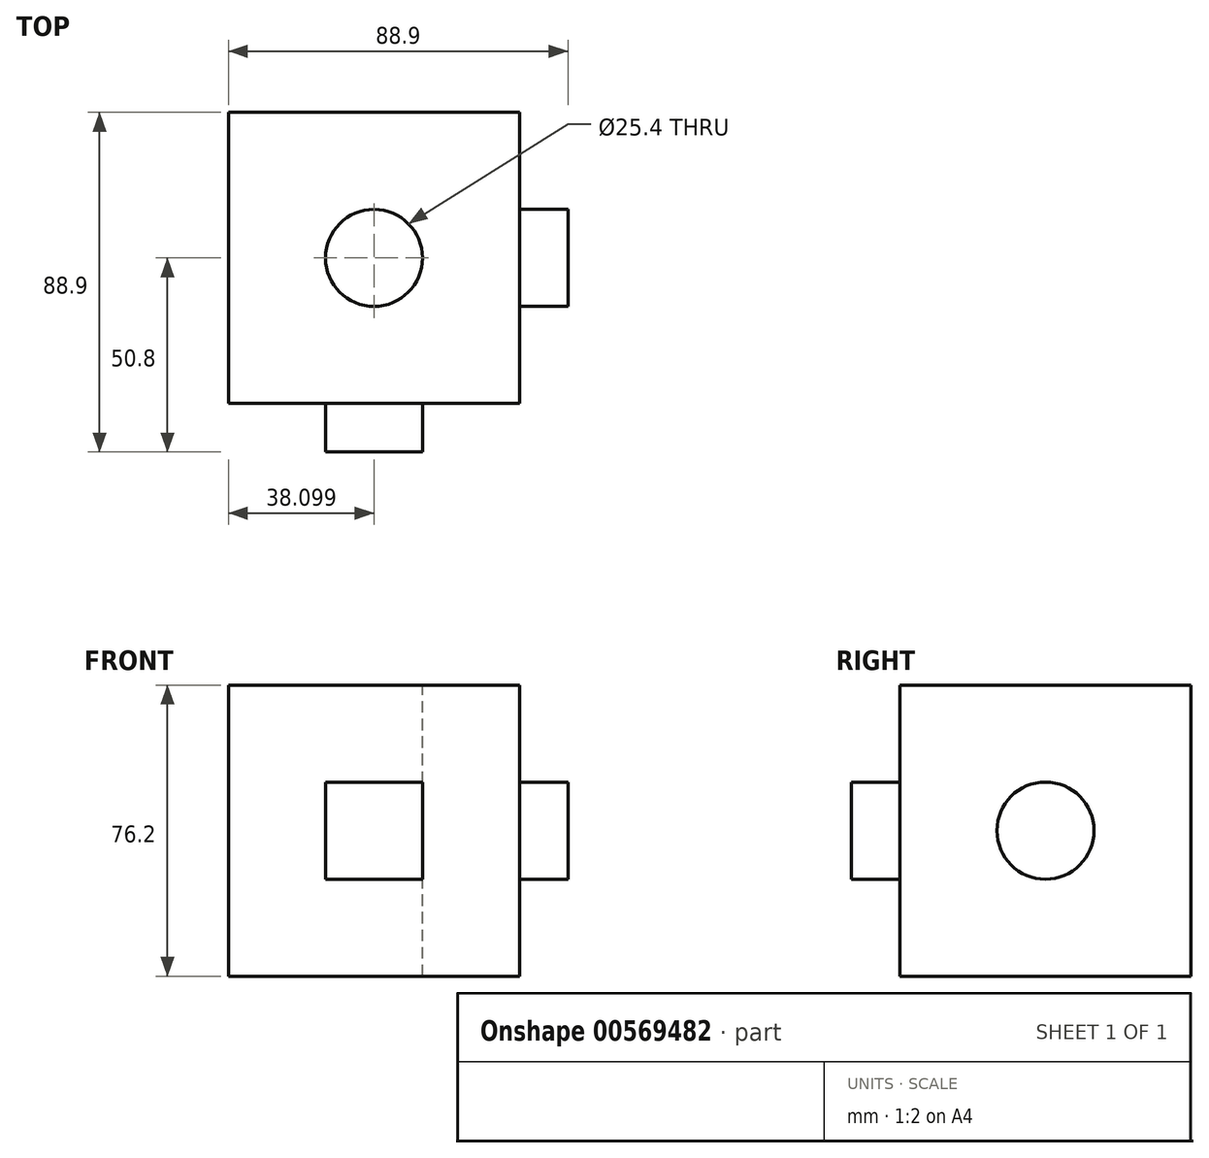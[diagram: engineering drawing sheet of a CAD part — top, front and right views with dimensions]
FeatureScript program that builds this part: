
annotation { "Feature Type Name" : "Feature", "Feature Type Description" : "" }
export const myFeature = defineFeature(function(context is Context, id is Id, definition is map)
    precondition{}
    {
        {
            var Q0;
            Q0=qCreatedBy(makeId("Front.planeOp"),FACE);
            var sketch = newSketch(context, id + "F0", { "sketchPlane" : qUnion([Q0])});
            skLineSegment(sketch, "E0.bottom", {"start": v(-26.71, 108.82) * mm, "end": v(49.49, 108.82) * mm});
            skLineSegment(sketch, "E0.top", {"start": v(-26.71, 32.62) * mm, "end": v(49.49, 32.62) * mm});
            skLineSegment(sketch, "E0.left", {"start": v(-26.71, 108.82) * mm, "end": v(-26.71, 32.62) * mm});
            skLineSegment(sketch, "E0.right", {"start": v(49.49, 108.82) * mm, "end": v(49.49, 32.62) * mm});
            skSolve(sketch);
        }
        {
            var Q0;
            Q0=makeQuery(id+"F0.imprint","IMPRINT",FACE,{"disambiguationData":[TD([[makeQuery(id+"F0.imprint","IMPRINT",EDGE,{"derivedFrom":sQuery(id+"F0.wireOp",EDGE,"E0.bottom")}),-1.0]])]});
            extrude(context, id + "F1", {"entities" : qUnion([Q0]), "depth" : 76.2 * mm, "offsetDistance" : 25.4 * mm});
        }
        {
            var Q0;
            Q0=makeQuery(id+"F1.opExtrude","CAP_FACE",FACE,{"disambiguationData":[OSD([sQuery(id+"F0.wireOp",EDGE,"E0.bottom"),sQuery(id+"F0.wireOp",EDGE,"E0.top"),sQuery(id+"F0.wireOp",EDGE,"E0.left"),sQuery(id+"F0.wireOp",EDGE,"E0.right")])],"isStart":false});
            var sketch = newSketch(context, id + "F2", { "sketchPlane" : qUnion([Q0])});
            skLineSegment(sketch, "E1.bottom", {"start": v(-1.31, 83.42) * mm, "end": v(24.09, 83.42) * mm});
            skLineSegment(sketch, "E1.top", {"start": v(-1.31, 58.02) * mm, "end": v(24.09, 58.02) * mm});
            skLineSegment(sketch, "E1.left", {"start": v(-1.31, 83.42) * mm, "end": v(-1.31, 58.02) * mm});
            skLineSegment(sketch, "E1.right", {"start": v(24.09, 83.42) * mm, "end": v(24.09, 58.02) * mm});
            skSolve(sketch);
        }
        {
            var Q0;
            Q0=makeQuery(id+"F2.imprint","IMPRINT",FACE,{"disambiguationData":[TD([[makeQuery(id+"F2.imprint","IMPRINT",EDGE,{"derivedFrom":sQuery(id+"F2.wireOp",EDGE,"E1.bottom")}),-1.0]])]});
            extrude(context, id + "F3", {"entities" : qUnion([Q0]), "operationType" : NewBodyOperationType.ADD, "depth" : 12.7 * mm, "offsetDistance" : 25.4 * mm});
        }
        {
            var Q0;
            Q0=makeQuery(id+"F1.opExtrude","SWEPT_FACE",FACE,{"disambiguationData":[OSD([sQuery(id+"F0.wireOp",EDGE,"E0.right")])]});
            var sketch = newSketch(context, id + "F4", { "sketchPlane" : qUnion([Q0])});
            skCircle(sketch, "E2", {"center": v(-38.1, 70.72) * mm, "radius": 12.7 * mm});
            skSolve(sketch);
        }
        {
            var Q0;
            Q0 = qSketchRegion(id + "F4", true);
            extrude(context, id + "F5", {"entities" : qUnion([Q0]), "operationType" : NewBodyOperationType.ADD, "depth" : 12.7 * mm, "offsetDistance" : 25.4 * mm});
        }
        {
            var Q0;
            Q0=makeQuery(id+"F1.opExtrude","SWEPT_FACE",FACE,{"disambiguationData":[OSD([sQuery(id+"F0.wireOp",EDGE,"E0.bottom")])]});
            var sketch = newSketch(context, id + "F6", { "sketchPlane" : qUnion([Q0])});
            skPoint(sketch, "E3", {"position": v(11.39, -38.1) * mm});
            skPoint(sketch, "E3.positionSnap0", {"position": v(11.39, -76.2) * mm});
            skPoint(sketch, "E3.positionSnap1", {"position": v(49.49, -38.1) * mm});
            skSolve(sketch);
        }
        {
            var Q0;
            Q0=sQuery(id+"F6.wireOp",VERTEX,"E3");
            var Q1;
            Q1=makeQuery(id+"F1.opExtrude","SWEPT_BODY",BODY,{"disambiguationData":[OSD([sQuery(id+"F0.wireOp",EDGE,"E0.bottom"),sQuery(id+"F0.wireOp",EDGE,"E0.top"),sQuery(id+"F0.wireOp",EDGE,"E0.left"),sQuery(id+"F0.wireOp",EDGE,"E0.right")])]});
            hole(context, id + "F7", {"style" : HoleStyle.SIMPLE, "endStyle" : HoleEndStyle.THROUGH, "holeDiameter" : 25.4 * mm, "isTappedThrough" : true, "tappedDepth" : 12.7 * mm, "tapClearance" : 3, "locations" : qUnion([Q0]), "scope" : qUnion([Q1])});
        }
    });
